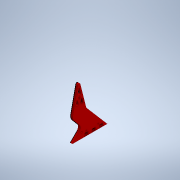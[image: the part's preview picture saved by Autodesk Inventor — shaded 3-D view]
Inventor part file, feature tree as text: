
AUTODESK INVENTOR PART (.ipt)
format: ipt  version: 2020 (Build 240168000, 168)  size: 520,704 bytes
history: native  units: mm
features: fillet x4, extrude x3, sketch x2, projected_geometry x1
ambient origin geometry x8: Origin, YZ Plane, XZ Plane, XY Plane, X Axis, Y Axis, Z Axis, Center Point
bodies: Solid1 (feature_tree)
feature tree (10):
  extrude  "Extrusion1"  Depth=27.0mm
  extrude  "Extrusion9"  Depth=27.8mm
  fillet  "Fillet2"  Radius=50.45mm
  fillet  "Fillet3"  Radius=10.0mm
  extrude  "Extrusion8"  Depth=4.8mm
  fillet  "Fillet4"  Radius=6.8mm
  fillet  "Fillet5"  Radius=1.6mm
  sketch  "Sketch1"  dims[d0=45.0deg d1=27.0mm]
  sketch  "Sketch8"  dims[d5=5.0mm d6=0.0mm d34=27.8mm d40=50.45mm d47=10.0mm d55=4.8mm d56=6.8mm d57=1.6mm d58=30.0mm d60=16.333333mm d61=10.0mm d63=10.0mm d65=5.0mm d66=14.45mm d67=104.9mm d72=3.0mm d75=0.5mm d76=3.6mm d77=12.0mm d78=20.0mm d79=0.0mm d80=0.0mm d81=49.0mm d88=1.5mm d98=3.0mm d99=0.0mm d100=14.45mm d102=76.0mm d103=3.1mm d104=10.0mm d105=30.0mm d106=3.1mm d108=56.0mm d109=10.0mm d110=3.0mm d111=3.0mm d112=1.5mm d113=3.0mm d114=3.0mm d115=1.5mm d116=1.5mm d117=1.0mm d50=0.5mm d51=0.872665mm d52=0.5mm d53=0.872665mm]
  projected_geometry  "Projected Loop6"
